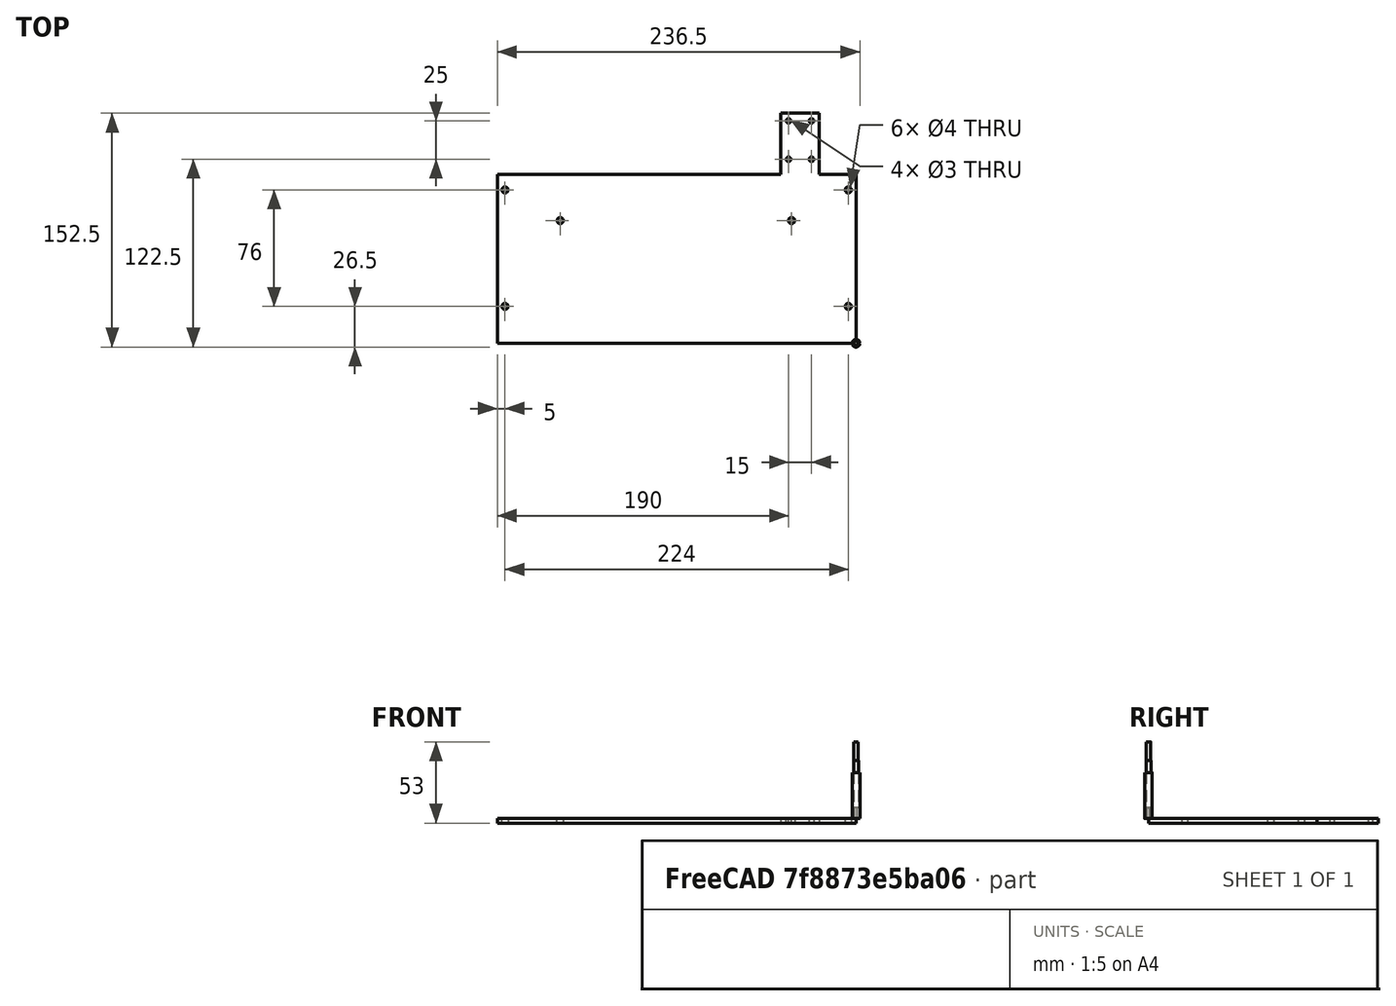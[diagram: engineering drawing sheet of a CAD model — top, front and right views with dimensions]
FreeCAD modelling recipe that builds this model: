
FCSTD DOCUMENT  (FreeCAD 0.20R29603 (Git))
Label: Ізоляція для БЖ (CNC 3018 PLUS)
License: All rights reserved
LicenseURL: http://en.wikipedia.org/wiki/All_rights_reserved
objects: Part::FeaturePython×4, Path::FeaturePython×4, App::DocumentObjectGroup×3, Mesh::FeaturePython×2, Sketcher::SketchObject×1, PartDesign::Pad×1, PartDesign::Body×1, App::FeaturePython×1
note: 10 computed .brp shape members not serialized (recipe doc carries the construction recipe); baked Part::Feature solids carry a one-line shape summary decoded from their .brp

FEATURE [Sketcher::SketchObject] Sketch
  FullyConstrained = false
  MapMode = 5
  Support = -> [XY_Plane]
  sketch-geometry (19):
    g0: LineSegment StartX=-234 StartY=110 StartZ=0 EndX=-49 EndY=110 EndZ=0
    g1: LineSegment StartX=0 StartY=110 StartZ=0 EndX=0 EndY=0 EndZ=0
    g2: LineSegment StartX=0 StartY=0 StartZ=0 EndX=-234 EndY=0 EndZ=0
    g3: LineSegment StartX=-234 StartY=0 StartZ=0 EndX=-234 EndY=110 EndZ=0
    g4: Circle CenterX=-193 CenterY=80 CenterZ=0 NormalX=0 NormalY=0 NormalZ=1 AngleXU=0 Radius=2
    g5: Circle CenterX=-42 CenterY=80 CenterZ=0 NormalX=0 NormalY=0 NormalZ=1 AngleXU=0 Radius=2
    g6: Circle CenterX=-229 CenterY=100 CenterZ=0 NormalX=0 NormalY=0 NormalZ=1 AngleXU=0 Radius=2
    g7: Circle CenterX=-5 CenterY=100 CenterZ=0 NormalX=0 NormalY=0 NormalZ=1 AngleXU=0 Radius=2
    g8: Circle CenterX=-229 CenterY=24 CenterZ=0 NormalX=0 NormalY=0 NormalZ=1 AngleXU=0 Radius=2
    g9: Circle CenterX=-5 CenterY=24 CenterZ=0 NormalX=0 NormalY=0 NormalZ=1 AngleXU=0 Radius=2
    g10: LineSegment StartX=-49 StartY=150 StartZ=0 EndX=-24 EndY=150 EndZ=0
    g11: LineSegment StartX=-24 StartY=150 StartZ=0 EndX=-24 EndY=110 EndZ=0
    g12: LineSegment StartX=-24 StartY=110 StartZ=0 EndX=-24.1247 EndY=110 EndZ=0
    g13: LineSegment StartX=-49 StartY=110 StartZ=0 EndX=-49 EndY=150 EndZ=0
    g14: Circle CenterX=-44 CenterY=145 CenterZ=0 NormalX=0 NormalY=0 NormalZ=1 AngleXU=0 Radius=1.5
    g15: Circle CenterX=-29 CenterY=145 CenterZ=0 NormalX=0 NormalY=0 NormalZ=1 AngleXU=0 Radius=1.5
    g16: Circle CenterX=-44 CenterY=120 CenterZ=0 NormalX=0 NormalY=0 NormalZ=1 AngleXU=0 Radius=1.5
    g17: Circle CenterX=-29 CenterY=120 CenterZ=0 NormalX=0 NormalY=0 NormalZ=1 AngleXU=0 Radius=1.5
    g18: LineSegment StartX=-24.1247 StartY=110 StartZ=0 EndX=0 EndY=110 EndZ=0
  constraints (54):
    c: Coincident(g1,g2)
    c: Coincident(g2,g3)
    c: Coincident(g3,g0)
    c: Horizontal(g0)
    c: Horizontal(g2)
    c: Vertical(g1)
    c: Vertical(g3)
    c: Coincident(g1,g-1)
    c: DistanceX(g0,g1) = 234
    c: DistanceY(g1,g1) = 110
    c: Distance(g4,g3) = 41
    c: Distance(g4,g0) = 30
    c: Distance(g5,g0) = 30
    c: Diameter(g5) = 4
    c: Diameter(g4) = 4
    c: Distance(g6,g0) = 10
    c: Distance(g6,g3) = 5
    c: Distance(g7,g1) = 5
    c: Distance(g7,g0) = 10
    c: Diameter(g6) = 4
    c: Diameter(g7) = 4
    c: Diameter(g9) = 4
    c: Diameter(g8) = 4
    c: Distance(g8,g3) = 5
    c: Distance(g9,g1) = 5
    c: Distance(g6,g8) = 76
    c: Distance(g7,g9) = 76
    c: Distance(g4,g5) = 151
    c: Coincident(g10,g11)
    c: Coincident(g11,g12)
    c: Coincident(g13,g10)
    c: Horizontal(g10)
    c: Horizontal(g12)
    c: Vertical(g11)
    c: Vertical(g13)
    c: PointOnObject(g11,g0)
    c: DistanceX(g10,g10) = 25
    c: Distance(g10,g11) = 40
    c: Diameter(g14) = 3
    c: Diameter(g15) = 3
    c: Diameter(g17) = 3
    c: Diameter(g16) = 3
    c: Distance(g14,g13) = 5
    c: Distance(g16,g13) = 5
    c: Distance(g15,g11) = 5
    c: Distance(g17,g11) = 5
    c: Distance(g14,g10) = 5
    c: Distance(g15,g10) = 5
    c: Distance(g17,g0) = 10
    c: Distance(g16,g0) = 10
    c: Distance(g0,g13) = 185
    c: Coincident(g18,g1)
    c: Horizontal(g18)
    c: PointOnObject(g12,g18)
FEATURE [PartDesign::Pad] Pad
  Direction = (0,0,1)
  Length = 3
  Length2 = 10
  Profile = -> Sketch
  ReferenceAxis = -> Sketch [N_Axis]
  Reversed = true
  Type = 0
FEATURE [PartDesign::Body] Body
  Group = -> [Sketch,Pad]
  Origin = -> Origin
  Tip = -> Pad
FEATURE [App::FeaturePython] SetupSheet  # Path/CAM operation (typed FeaturePython)
  ClearanceHeightExpression = OpStockZMax+SetupSheet.ClearanceHeightOffset
  ClearanceHeightOffset = 5
  CoolantMode = 0
  CoolantModes = None | Flood | Mist
  FinalDepthExpression = OpFinalDepth
  HorizRapid = 0
  SafeHeightExpression = OpStockZMax+SetupSheet.SafeHeightOffset
  SafeHeightOffset = 3
  StartDepthExpression = OpStartDepth
  StepDownExpression = OpToolDiameter
  VertRapid = 0
FEATURE [Part::FeaturePython] Clone  label="Model-Body"  # Draft clone (typed FeaturePython)
  AttacherType = Attacher::AttachEngine3D
  Fuse = false
  Objects = -> [Body]
  PathResource = Model
  Scale = (1,1,1)
FEATURE [App::DocumentObjectGroup] Model
  Group = -> [Clone]
FEATURE [Part::FeaturePython] ToolBit  label="Endmill"  # Path/CAM toolbit (typed FeaturePython)
  BitPropertyNames = Chipload | CuttingEdgeHeight | Diameter | Flutes | Length | Material | ShankDiameter | SpindleDirection
  BitShape = <path>
  Chipload = 0
  CuttingEdgeHeight = 30
  Diameter = 5
  Flutes = 0
  Length = 50
  Material = 0
  ShankDiameter = 3
  ShapeName = endmill
  SpindleDirection = 0
FEATURE [Part::FeaturePython] ToolBit003  label="kukuruza-1.7-7-3.175"  # Path/CAM toolbit (typed FeaturePython)
  BitPropertyNames = Chipload | CuttingEdgeHeight | Diameter | Flutes | Length | Material | ShankDiameter | SpindleDirection
  BitShape = <path>
  Chipload = 0
  CuttingEdgeHeight = 7
  Diameter = 1.7
  File = <userpath>/FreeCAD/toolbits/Bit/kukuruza-1.7-7-3.fctb
  Flutes = 0
  Length = 38
  Material = 0
  ShankDiameter = 3.17
  ShapeName = endmill
  SpindleDirection = 0
FEATURE [Path::FeaturePython] TC__kukuruza_1_7_7_3_175  label="kukuruza-1.7-7-3.176"  # Path/CAM operation (typed FeaturePython)
  HorizFeed = 100
  HorizRapid = 300
  SpindleDir = 0
  SpindleSpeed = 1000
  Tool = -> ToolBit003
  ToolNumber = 1
  VertFeed = 200
  VertRapid = 300
FEATURE [App::DocumentObjectGroup] Tools
  Group = -> [TC__kukuruza_1_7_7_3_175]
FEATURE [Path::FeaturePython] Profile  label="Отверстия"  # Path/CAM operation (typed FeaturePython)
  Active = true
  AreaParams:
    Tolerance = 1e-07
    FitArcs = True
    Simplify = False
    CleanDistance = 0.0
    Accuracy = 0.01
    Unit = 1.0
    MinArcPoints = 4
    MaxArcPoints = 100
    ClipperScale = 10000000.0
    Fill = 0
    Coplanar = 0
    Reorient = True
    Outline = False
    Explode = False
    OpenMode = 0
    Deflection = 0.01
    SubjectFill = 0
    ClipFill = 0
    Offset = -0.85
    ExtraPass = 0
    Stepover = 0.0
    LastStepover = 0.0
    JoinType = 0
    EndType = 0
    MiterLimit = 2.0
    RoundPrecision = 0.0
    PocketMode = 0
    ToolRadius = 1.0
    PocketExtraOffset = 0.0
    PocketStepover = 0.0
    PocketLastStepover = 0.0
    FromCenter = False
    Angle = 45.0
    AngleShift = 0.0
    Shift = 0.0
    Thicken = False
    SectionCount = -1
    Stepdown = 1.0
    SectionOffset = 0.0
    SectionTolerance = 1e-06
    SectionMode = 2
    Project = False
  Base = -> [Clone]
  ClearanceHeight = 5
  CoolantMode = 0
  CycleTime = 00:00:25
  Direction = 0
  FinalDepth = -3
  HandleMultipleFeatures = 0
  JoinType = 0
  MiterLimit = 0.1
  OffsetExtra = 0
  OpFinalDepth = -3
  OpStartDepth = 0
  OpStockZMax = 0
  OpStockZMin = -3
  OpToolDiameter = 1.7
  PathParams = {'orientation': 1, 'feedrate': 100.0, 'feedrate_v': 200.0, 'verbose': True, 'resume_height': 3.0, 'retraction': 5.0, 'return_end': True, 'preamble': False}
  SafeHeight = 3
  Side = 1
  SplitArcs = false
  StartDepth = 0
  StartPoint = (0,0,0)
  StepDown = 0.3
  ToolController = -> TC__kukuruza_1_7_7_3_175
  UseComp = true
  UseStartPoint = false
  processCircles = false
  processHoles = false
  processPerimeter = true
  expr: ClearanceHeight = 5
  expr: FinalDepth = OpFinalDepth
  expr: SafeHeight = OpStockZMax + SetupSheet.SafeHeightOffset
  expr: StartDepth = OpStartDepth
FEATURE [Path::FeaturePython] Profile001  label="Обрезка"  # Path/CAM operation (typed FeaturePython)
  Active = true
  AreaParams:
    Tolerance = 1e-07
    FitArcs = True
    Simplify = False
    CleanDistance = 0.0
    Accuracy = 0.01
    Unit = 1.0
    MinArcPoints = 4
    MaxArcPoints = 100
    ClipperScale = 10000000.0
    Fill = 0
    Coplanar = 0
    Reorient = True
    Outline = False
    Explode = False
    OpenMode = 0
    Deflection = 0.01
    SubjectFill = 0
    ClipFill = 0
    Offset = 0.85
    ExtraPass = 0
    Stepover = 0.0
    LastStepover = 0.0
    JoinType = 0
    EndType = 0
    MiterLimit = 2.0
    RoundPrecision = 0.0
    PocketMode = 0
    ToolRadius = 1.0
    PocketExtraOffset = 0.0
    PocketStepover = 0.0
    PocketLastStepover = 0.0
    FromCenter = False
    Angle = 45.0
    AngleShift = 0.0
    Shift = 0.0
    Thicken = False
    SectionCount = -1
    Stepdown = 1.0
    SectionOffset = 0.0
    SectionTolerance = 1e-06
    SectionMode = 2
    Project = False
  Base = -> [Clone]
  ClearanceHeight = 5
  CoolantMode = 0
  CycleTime = 00:01:17
  Direction = 0
  FinalDepth = -3
  HandleMultipleFeatures = 0
  JoinType = 0
  MiterLimit = 0.1
  OffsetExtra = 0
  OpFinalDepth = -3
  OpStartDepth = 0
  OpStockZMax = 0
  OpStockZMin = -3
  OpToolDiameter = 1.7
  PathParams = {'orientation': 1, 'feedrate': 100.0, 'feedrate_v': 200.0, 'verbose': True, 'resume_height': 3.0, 'retraction': 5.0, 'return_end': True, 'preamble': False}
  SafeHeight = 3
  Side = 0
  SplitArcs = false
  StartDepth = 0
  StartPoint = (0,0,0)
  StepDown = 0.3
  ToolController = -> TC__kukuruza_1_7_7_3_175
  UseComp = true
  UseStartPoint = false
  processCircles = false
  processHoles = false
  processPerimeter = true
  expr: ClearanceHeight = 5
  expr: FinalDepth = OpFinalDepth
  expr: SafeHeight = OpStockZMax + SetupSheet.SafeHeightOffset
  expr: StartDepth = OpStartDepth
FEATURE [App::DocumentObjectGroup] Operations
  Group = -> [Profile,Profile001]
FEATURE [Mesh::FeaturePython] CutMaterial  # WARN: FeaturePython — macro-defined, semantics opaque (R4)
FEATURE [Mesh::FeaturePython] CutMaterial001  # WARN: FeaturePython — macro-defined, semantics opaque (R4)
FEATURE [Part::FeaturePython] Clone001  label="Stock-Body"  # Draft clone (typed FeaturePython)
  AttacherType = Attacher::AttachEngine3D
  Fuse = false
  Objects = -> [Body]
  PathResource = Stock
  Scale = (1,1,1)
  StockType = Unknown
FEATURE [Path::FeaturePython] Job  # Path/CAM operation (typed FeaturePython)
  CycleTime = 00:01:42
  Fixtures = G59
  GeometryTolerance = 0.01
  JobType = 0
  LastPostProcessDate = 2023-05-26 00:00:41.979804
  LastPostProcessOutput = <userpath>/Gcode/1
  Model = -> Model
  Operations = -> Operations
  OrderOutputBy = 0
  PostProcessor = 11
  SetupSheet = -> SetupSheet
  SplitOutput = false
  Stock = -> Clone001
  Tools = -> Tools
note: 2 file-system paths scrubbed to <path> (originals preserved in the JSON sidecar)
